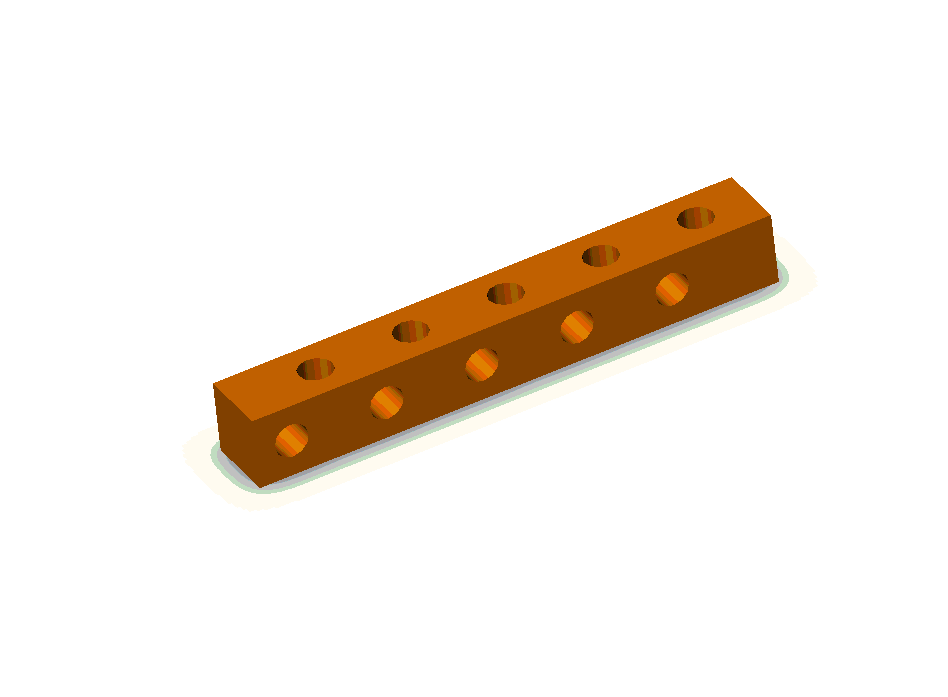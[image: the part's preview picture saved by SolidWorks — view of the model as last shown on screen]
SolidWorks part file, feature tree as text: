
SOLIDWORKS PART (.sldprt)
format: sldprt  version: not decoded by parser v0  size: 129,536 bytes
history: native  units: mm
features: sketch x3, cut_extrude x2, pattern_linear x2, extrude x1 (+8 scaffold rows collapsed)
feature tree (16):
  scaffold x8  (default folders/planes/origin — collapsed)
  sketch  "Sketch1"  dims[D1=4.7625mm D2=4.7625mm]
  extrude  "Base-Extrude"  Depth=34.655mm
  sketch  "Sketch2"  dims[D1=2.2606mm D2=~2.38125mm D3=~2.38125mm D4=9.525mm]
  cut_extrude  "Cut-Extrude1"  [1 undecoded]
  pattern_linear  "LPattern1"  Count1=5 Count2=1 Spacing1=6.35mm Spacing2=50mm
  sketch  "Sketch4"  dims[D2=2.2606mm D1=3.175mm D3=~2.38125mm]
  cut_extrude  "Cut-Extrude2"  [1 undecoded]
  pattern_linear  "LPattern2"  Count1=5 Count2=1 Spacing1=6.35mm Spacing2=50mm
decode coverage: 6 of 8 modeling features carry decoded parameters
note: ~ marks probable driven/reference dimensions
note: 2 parameter values undecoded
note: suppression state not decoded; provenance and decode notes live in map.json
